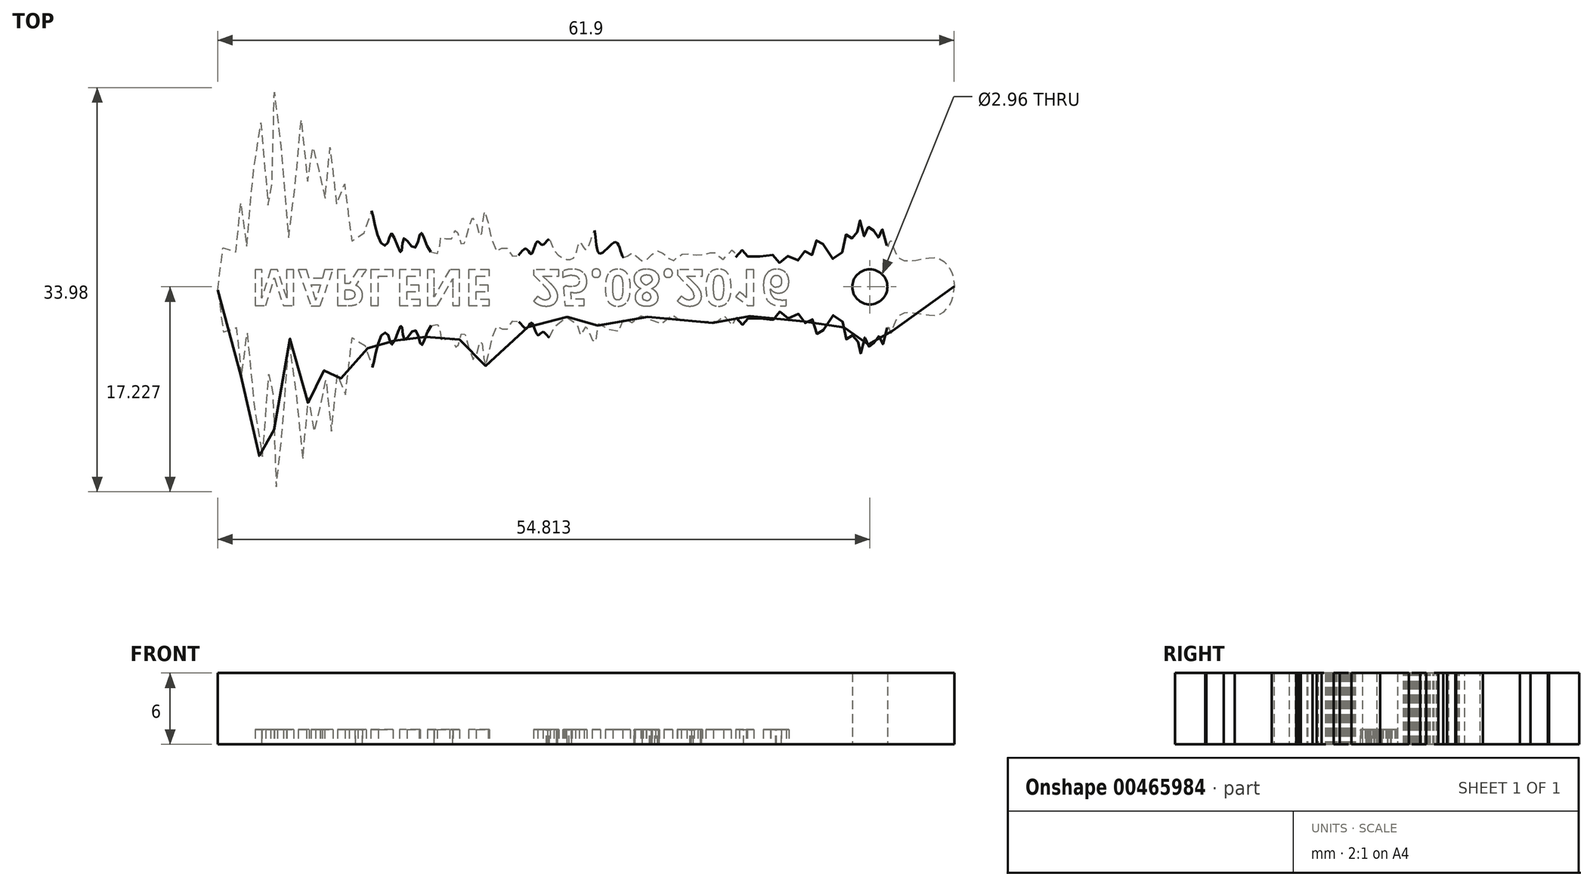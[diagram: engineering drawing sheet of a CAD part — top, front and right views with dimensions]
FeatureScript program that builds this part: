
annotation { "Feature Type Name" : "Feature", "Feature Type Description" : "" }
export const myFeature = defineFeature(function(context is Context, id is Id, definition is map)
    precondition{}
    {
        {
            var Q0;
            Q0=qCreatedBy(makeId("Top.planeOp"),FACE);
            var sketch = newSketch(context, id + "F0", { "sketchPlane" : qUnion([Q0])});
            skFitSpline(sketch, "E0.MirrorCS", {"points": [v(-21.5, 3.1) * mm, v(-21.04, 6.62) * mm, v(-20.24, 5.36) * mm, v(-19.59, 10.5) * mm, v(-19.08, 6.73) * mm, v(-18.01, 17.57) * mm, v(-17.1, 8.96) * mm, v(-16.67, 20.11) * mm, v(-15.44, 7.24) * mm, v(-14.54, 17.5) * mm, v(-13.85, 11.8) * mm, v(-13.35, 16.03) * mm, v(-12.62, 9.95) * mm, v(-12.1, 15.13) * mm, v(-11.4, 10.05) * mm, v(-10.88, 12.02) * mm, v(-10.07, 6.7) * mm, v(-9.39, 7.76) * mm, v(-8.97, 8.1) * mm, v(-8.6, 9.77) * mm, v(-7.9, 7.27) * mm, v(-7.29, 6.92) * mm, v(-6.89, 7.83) * mm, v(-6.1, 6.24) * mm, v(-5.84, 7.44) * mm, v(-4.98, 6.62) * mm, v(-4.43, 7.91) * mm, v(-3.68, 6.39) * mm, v(-2.94, 6.28) * mm, v(-2.7, 7.6) * mm, v(-1.96, 7.28) * mm, v(-1.46, 8.2) * mm, v(-0.91, 6.8) * mm, v(-0.04, 9.17) * mm, v(0.6, 7.52) * mm, v(0.93, 9.7) * mm, v(1.93, 6.35) * mm, v(2.59, 6.76) * mm, v(3.46, 5.82) * mm, v(4.37, 6.57) * mm, v(4.84, 6.11) * mm, v(5.35, 7.16) * mm, v(5.79, 6.88) * mm, v(6.3, 7.35) * mm, v(6.82, 6.36) * mm, v(8.4, 5.8) * mm, v(8.92, 7.17) * mm, v(9.46, 6.48) * mm, v(10.15, 8.1) * mm, v(10.57, 6.16) * mm, v(11.95, 7.12) * mm, v(12.62, 5.79) * mm, v(13.29, 6.18) * mm, v(14.28, 5.5) * mm, v(15.47, 6.4) * mm, v(16.7, 5.56) * mm, v(17.42, 6.07) * mm, v(19.09, 6.03) * mm, v(20.38, 6.2) * mm, v(21, 5.67) * mm, v(21.8, 6.5) * mm, v(22.09, 5.79) * mm, v(22.7, 6.53) * mm, v(23.26, 5.68) * mm, v(24.91, 6.2) * mm, v(25.64, 5.36) * mm, v(26.34, 5.95) * mm, v(27.29, 5.58) * mm, v(27.89, 6.37) * mm, v(28.42, 6.03) * mm, v(28.94, 7.48) * mm, v(30.05, 5.82) * mm, v(30.91, 6.1) * mm, v(31.42, 7.91) * mm, v(32.05, 7.27) * mm, v(32.43, 9) * mm, v(32.9, 7.53) * mm, v(33.33, 8.68) * mm, v(33.9, 7.34) * mm, v(34.27, 8.28) * mm, v(34.8, 6.74) * mm, v(35.04, 7.26) * mm, v(35.8, 5.76) * mm, v(38.83, 5.8) * mm, v(40.18, 4.56) * mm, v(40.4, 3.39) * mm], "startDerivative": vector(11.4, 361.54) * mm, "endDerivative": vector(7.63, -119.86) * mm});
            skFitSpline(sketch, "E1.MirrorCS", {"points": [v(-21.5, 3.1) * mm, v(-21.04, 6.62) * mm, v(-20.24, 5.36) * mm, v(-19.59, 10.5) * mm, v(-19.08, 6.73) * mm, v(-18.01, 17.57) * mm, v(-17.1, 8.96) * mm, v(-16.67, 20.11) * mm, v(-15.44, 7.24) * mm, v(-14.54, 17.5) * mm, v(-13.85, 11.8) * mm, v(-13.35, 16.03) * mm, v(-12.62, 9.95) * mm, v(-12.1, 15.13) * mm, v(-11.4, 10.05) * mm, v(-10.88, 12.02) * mm, v(-10.07, 6.7) * mm, v(-9.39, 7.76) * mm, v(-8.97, 8.1) * mm, v(-8.6, 9.77) * mm, v(-7.9, 7.27) * mm, v(-7.29, 6.92) * mm, v(-6.89, 7.83) * mm, v(-6.1, 6.24) * mm, v(-5.84, 7.44) * mm, v(-4.98, 6.62) * mm, v(-4.43, 7.91) * mm, v(-3.68, 6.39) * mm, v(-2.94, 6.28) * mm, v(-2.7, 7.6) * mm, v(-1.96, 7.28) * mm, v(-1.46, 8.2) * mm, v(-0.91, 6.8) * mm, v(-0.04, 9.17) * mm, v(0.6, 7.52) * mm, v(0.93, 9.7) * mm, v(1.93, 6.35) * mm, v(2.59, 6.76) * mm, v(3.46, 5.82) * mm, v(4.37, 6.57) * mm, v(4.84, 6.11) * mm, v(5.35, 7.16) * mm, v(5.79, 6.88) * mm, v(6.3, 7.35) * mm, v(6.82, 6.36) * mm, v(8.4, 5.8) * mm, v(8.92, 7.17) * mm, v(9.46, 6.48) * mm, v(10.15, 8.1) * mm, v(10.57, 6.16) * mm, v(11.95, 7.12) * mm, v(12.62, 5.79) * mm, v(13.29, 6.18) * mm, v(14.28, 5.5) * mm, v(15.47, 6.4) * mm, v(16.7, 5.56) * mm, v(17.42, 6.07) * mm, v(19.09, 6.03) * mm, v(20.38, 6.2) * mm, v(21, 5.67) * mm, v(21.8, 6.5) * mm, v(22.09, 5.79) * mm, v(22.7, 6.53) * mm, v(23.26, 5.68) * mm, v(24.91, 6.2) * mm, v(25.64, 5.36) * mm, v(26.34, 5.95) * mm, v(27.29, 5.58) * mm, v(27.89, 6.37) * mm, v(28.42, 6.03) * mm, v(28.94, 7.48) * mm, v(30.05, 5.82) * mm, v(30.91, 6.1) * mm, v(31.42, 7.91) * mm, v(32.05, 7.27) * mm, v(32.43, 9) * mm, v(32.9, 7.53) * mm, v(33.33, 8.68) * mm, v(33.9, 7.34) * mm, v(34.27, 8.28) * mm, v(34.8, 6.74) * mm, v(35.04, 7.26) * mm, v(35.8, 5.76) * mm, v(38.83, 5.8) * mm, v(40.18, 4.56) * mm, v(40.4, 3.39) * mm], "startDerivative": vector(11.4, 361.54) * mm, "endDerivative": vector(7.63, -119.86) * mm});
            skLineSegment(sketch, "E2", {"start": v(-21.5, 3.1) * mm, "end": v(40.4, 3.39) * mm});
            skFitSpline(sketch, "E3.MirrorCS", {"points": [v(-21.5, 3.1) * mm, v(-21, -0.41) * mm, v(-20.22, 0.85) * mm, v(-19.52, -4.27) * mm, v(-19.05, -0.5) * mm, v(-17.87, -11.33) * mm, v(-17.05, -2.72) * mm, v(-16.52, -13.87) * mm, v(-15.4, -0.98) * mm, v(-14.4, -11.23) * mm, v(-13.77, -5.52) * mm, v(-13.23, -9.75) * mm, v(-12.56, -3.66) * mm, v(-11.98, -8.84) * mm, v(-11.34, -3.75) * mm, v(-10.8, -5.72) * mm, v(-10.03, -0.4) * mm, v(-9.35, -1.44) * mm, v(-8.92, -1.78) * mm, v(-8.54, -3.45) * mm, v(-7.86, -0.94) * mm, v(-7.25, -0.58) * mm, v(-6.84, -1.5) * mm, v(-6.07, 0.1) * mm, v(-5.8, -1.1) * mm, v(-4.95, -0.27) * mm, v(-4.39, -1.55) * mm, v(-3.65, -0.02) * mm, v(-2.9, 0.1) * mm, v(-2.65, -1.22) * mm, v(-1.92, -0.9) * mm, v(-1.42, -1.82) * mm, v(-0.88, -0.4) * mm, v(0.01, -2.77) * mm, v(0.63, -1.11) * mm, v(0.99, -3.3) * mm, v(1.96, 0.07) * mm, v(2.62, -0.33) * mm, v(3.48, 0.6) * mm, v(4.4, -0.13) * mm, v(4.86, 0.33) * mm, v(5.4, -0.71) * mm, v(5.82, -0.42) * mm, v(6.34, -0.9) * mm, v(6.85, 0.1) * mm, v(8.43, 0.68) * mm, v(8.96, -0.69) * mm, v(9.49, 0) * mm, v(10.2, -1.6) * mm, v(10.6, 0.34) * mm, v(11.98, -0.6) * mm, v(12.64, 0.73) * mm, v(13.32, 0.35) * mm, v(14.3, 1.03) * mm, v(15.5, 0.15) * mm, v(16.73, 1) * mm, v(17.45, 0.5) * mm, v(19.11, 0.55) * mm, v(20.4, 0.38) * mm, v(21.02, 0.93) * mm, v(21.82, 0.11) * mm, v(22.11, 0.82) * mm, v(22.72, 0.09) * mm, v(23.28, 0.94) * mm, v(24.94, 0.43) * mm, v(25.66, 1.28) * mm, v(26.37, 0.7) * mm, v(27.3, 1.08) * mm, v(27.92, 0.3) * mm, v(28.45, 0.63) * mm, v(28.98, -0.81) * mm, v(30.08, 0.87) * mm, v(30.94, 0.59) * mm, v(31.47, -1.22) * mm, v(32.09, -0.57) * mm, v(32.49, -2.3) * mm, v(32.95, -0.82) * mm, v(33.38, -1.96) * mm, v(33.95, -0.62) * mm, v(34.32, -1.55) * mm, v(34.83, -0.01) * mm, v(35.07, -0.53) * mm, v(35.83, 0.98) * mm, v(38.86, 0.97) * mm, v(40.2, 2.22) * mm, v(40.4, 3.39) * mm], "startDerivative": vector(14.8, -361.42) * mm, "endDerivative": vector(6.51, 119.93) * mm});
            skCircle(sketch, "E4", {"center": v(33.3, 3.36) * mm, "radius": 1.48 * mm});
            skSolve(sketch);
        }
        {
            var Q0;
            Q0 = qSketchRegion(id + "F0", true);
            var Q1;
            Q1=makeQuery(id+"F0.imprint","IMPRINT",FACE,{"disambiguationData":[TD([[makeQuery(id+"F0.imprint","IMPRINT",EDGE,{"derivedFrom":sQuery(id+"F0.wireOp",EDGE,"E1.MirrorCS")}),-1.0]])]});
            extrude(context, id + "F1", {"entities" : qUnion([Q0, Q1]), "depth" : 6 * mm});
        }
        {
            var Q0;
            Q0=makeQuery(id+"F1.opExtrude","CAP_FACE",FACE,{"disambiguationData":[OSD([sQuery(id+"F0.wireOp",EDGE,"E1.MirrorCS"),sQuery(id+"F0.wireOp",EDGE,"E3.MirrorCS"),sQuery(id+"F0.wireOp",EDGE,"E4")])],"isStart":true});
            var sketch = newSketch(context, id + "F2", { "sketchPlane" : qUnion([Q0])});
            skText(sketch, "E5", { "text": "MARLENE   25.08.2016", "fontName": "OpenSans-Bold.ttf"});
            const initialGuessF2  = {"E5": [-0.01873, -0.0048, 1, 0, 0.00305]};
            skSetInitialGuess(sketch, initialGuessF2);
            skSolve(sketch);
        }
        {
            var Q0;
            Q0 = qSketchRegion(id + "F2", true);
            extrude(context, id + "F3", {"entities" : qUnion([Q0]), "operationType" : NewBodyOperationType.REMOVE, "oppositeDirection" : true, "depth" : 1.25 * mm});
        }
    });
